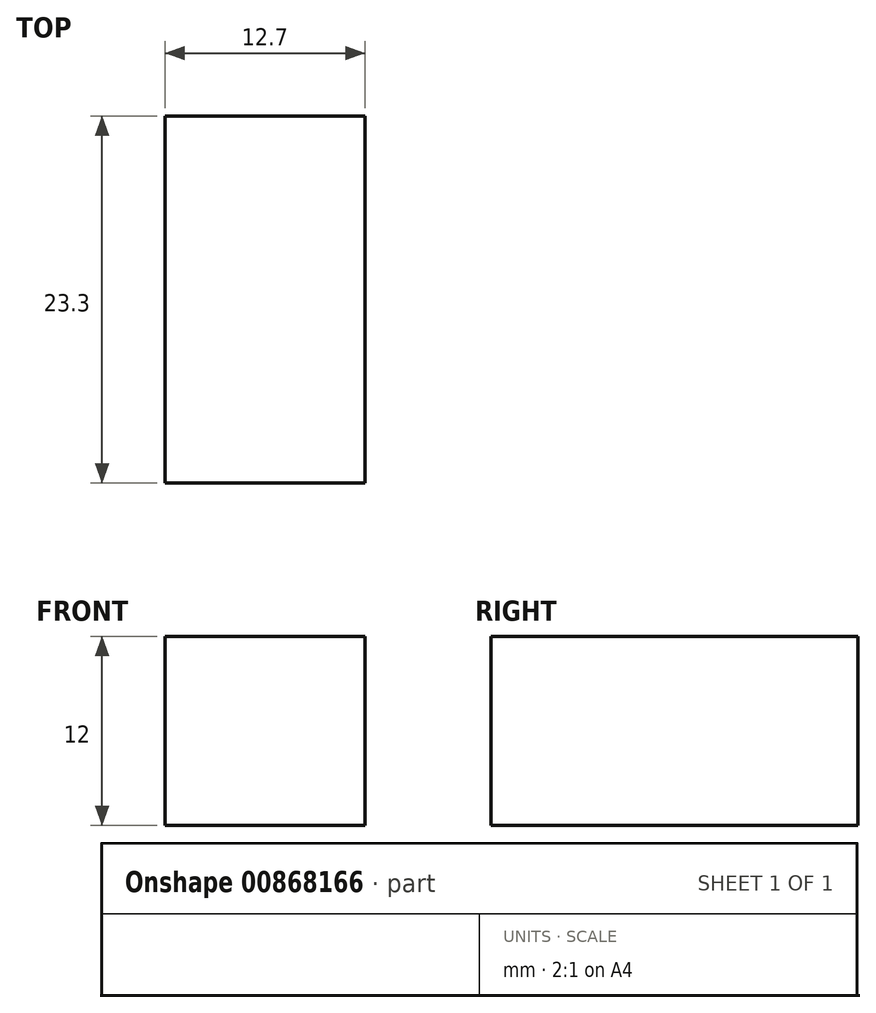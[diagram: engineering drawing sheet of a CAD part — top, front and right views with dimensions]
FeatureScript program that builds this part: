
annotation { "Feature Type Name" : "Feature", "Feature Type Description" : "" }
export const myFeature = defineFeature(function(context is Context, id is Id, definition is map)
    precondition{}
    {
        {
            var Q0;
            Q0=qCreatedBy(makeId("Top.planeOp"),FACE);
            var sketch = newSketch(context, id + "F0", { "sketchPlane" : qUnion([Q0])});
            skLineSegment(sketch, "E0.bottom", {"start": v(0, 0) * mm, "end": v(12.7, 0) * mm});
            skLineSegment(sketch, "E0.top", {"start": v(0, 23.3) * mm, "end": v(12.7, 23.3) * mm});
            skLineSegment(sketch, "E0.left", {"start": v(0, 0) * mm, "end": v(0, 23.3) * mm});
            skLineSegment(sketch, "E0.right", {"start": v(12.7, 0) * mm, "end": v(12.7, 23.3) * mm});
            skSolve(sketch);
        }
        {
            var Q0;
            Q0 = qSketchRegion(id + "F0", true);
            extrude(context, id + "F1", {"entities" : qUnion([Q0]), "depth" : 12 * mm, "offsetDistance" : 25 * mm});
        }
    });
